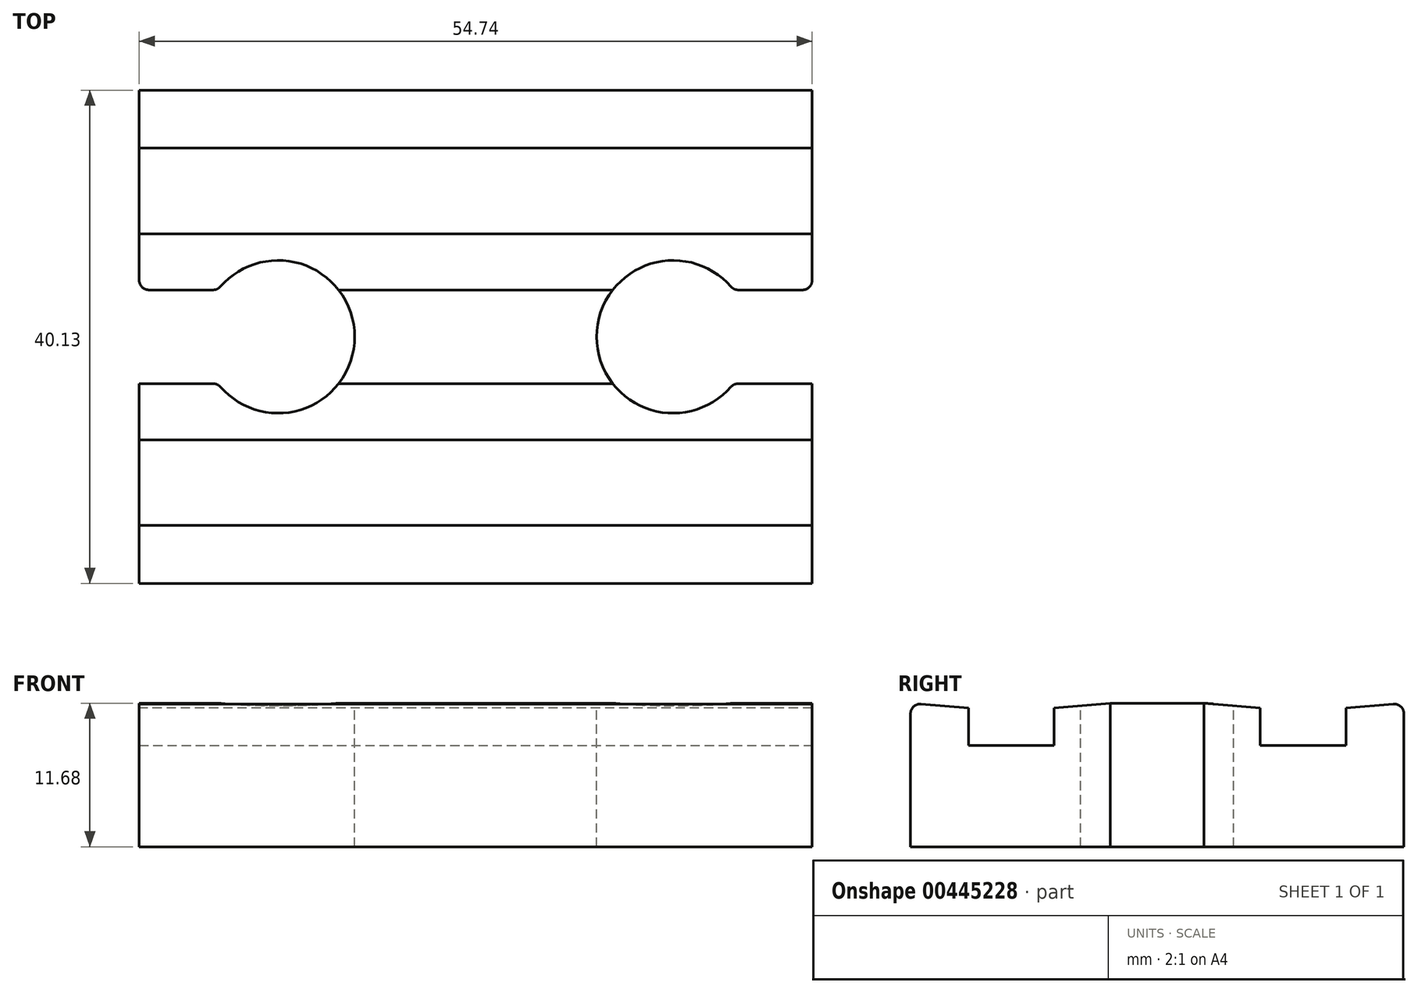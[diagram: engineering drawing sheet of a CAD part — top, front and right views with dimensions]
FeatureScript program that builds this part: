
annotation { "Feature Type Name" : "Feature", "Feature Type Description" : "" }
export const myFeature = defineFeature(function(context is Context, id is Id, definition is map)
    precondition{}
    {
        {
            var Q0;
            Q0=qCreatedBy(makeId("Top.planeOp"),FACE);
            var sketch = newSketch(context, id + "F0", { "sketchPlane" : qUnion([Q0])});
            skLineSegment(sketch, "E0.bottom", {"start": v(0, 0) * mm, "end": v(54.74, 0) * mm});
            skLineSegment(sketch, "E0.top", {"start": v(0, 40.13) * mm, "end": v(54.74, 40.13) * mm});
            skLineSegment(sketch, "E0.left", {"start": v(0, 0) * mm, "end": v(0, 40.13) * mm});
            skLineSegment(sketch, "E0.right", {"start": v(54.74, 0) * mm, "end": v(54.74, 40.13) * mm});
            skSolve(sketch);
        }
        {
            var Q0;
            Q0 = qSketchRegion(id + "F0", true);
            extrude(context, id + "F1", {"entities" : qUnion([Q0]), "depth" : 11.68 * mm});
        }
        {
            var Q0;
            Q0=makeQuery(id+"F1.opExtrude","SWEPT_FACE",FACE,{"disambiguationData":[OSD([sQuery(id+"F0.wireOp",EDGE,"E0.right")])]});
            var sketch = newSketch(context, id + "F2", { "sketchPlane" : qUnion([Q0])});
            skLineSegment(sketch, "E1.bottom", {"start": v(35.4, 11.68) * mm, "end": v(28.45, 11.68) * mm});
            skLineSegment(sketch, "E1.top", {"start": v(35.4, 8.26) * mm, "end": v(28.45, 8.26) * mm});
            skLineSegment(sketch, "E1.left", {"start": v(35.4, 11.68) * mm, "end": v(35.4, 8.26) * mm});
            skLineSegment(sketch, "E1.right", {"start": v(28.45, 11.68) * mm, "end": v(28.45, 8.26) * mm});
            skLineSegment(sketch, "E2", {"start": v(20.07, 11.68) * mm, "end": v(20.07, 0) * mm, "construction": true});
            skLineSegment(sketch, "E3.MirrorCS", {"start": v(11.68, 11.68) * mm, "end": v(11.68, 8.26) * mm});
            skLineSegment(sketch, "E4.MirrorCS", {"start": v(4.72, 11.68) * mm, "end": v(11.68, 11.68) * mm});
            skLineSegment(sketch, "E5.MirrorCS", {"start": v(4.72, 8.26) * mm, "end": v(11.68, 8.26) * mm});
            skLineSegment(sketch, "E6.MirrorCS", {"start": v(4.72, 11.68) * mm, "end": v(4.72, 8.26) * mm});
            skSolve(sketch);
        }
        {
            var Q0;
            Q0 = qSketchRegion(id + "F2", true);
            extrude(context, id + "F3", {"entities" : qUnion([Q0]), "operationType" : NewBodyOperationType.REMOVE, "endBound" : BoundingType.THROUGH_ALL, "oppositeDirection" : true, "depth" : 25.4 * mm});
        }
        {
            var Q0;
            Q0=makeQuery(id+"F1.opExtrude","SWEPT_FACE",FACE,{"disambiguationData":[OSD([sQuery(id+"F0.wireOp",EDGE,"E0.right")])]});
            var sketch = newSketch(context, id + "F4", { "sketchPlane" : qUnion([Q0])});
            skLineSegment(sketch, "E7", {"start": v(0, 11.68) * mm, "end": v(4.72, 11.29) * mm});
            skLineSegment(sketch, "E8", {"start": v(40.13, 11.68) * mm, "end": v(35.4, 11.29) * mm});
            skLineSegment(sketch, "E9", {"start": v(0, 11.68) * mm, "end": v(4.72, 11.68) * mm});
            skLineSegment(sketch, "E10", {"start": v(4.72, 11.68) * mm, "end": v(4.72, 11.29) * mm});
            skLineSegment(sketch, "E11", {"start": v(35.4, 11.29) * mm, "end": v(35.4, 11.68) * mm});
            skLineSegment(sketch, "E12", {"start": v(35.4, 11.68) * mm, "end": v(40.13, 11.68) * mm});
            skSolve(sketch);
        }
        {
            var Q0;
            Q0 = qSketchRegion(id + "F4", true);
            extrude(context, id + "F5", {"entities" : qUnion([Q0]), "operationType" : NewBodyOperationType.REMOVE, "endBound" : BoundingType.THROUGH_ALL, "oppositeDirection" : true, "depth" : 25.4 * mm});
        }
        {
            var Q0;
            {var subQ0=sQuery(id+"F0.wireOp",EDGE,"E0.left");var subQ1=sQuery(id+"F0.wireOp",EDGE,"E0.right");Q0=makeQuery(id+"F3.boolean.opBoolean","SPLIT",FACE,{"disambiguationData":[TD([makeQuery(id+"F3.opExtrude","SWEPT_FACE",FACE,{"disambiguationData":[OSD([sQuery(id+"F2.wireOp",EDGE,"E1.right")])]})])],"derivedFrom":makeQuery(id+"F1.opExtrude","CAP_FACE",FACE,{"disambiguationData":[OSD([sQuery(id+"F0.wireOp",EDGE,"E0.bottom"),sQuery(id+"F0.wireOp",EDGE,"E0.top"),subQ0,subQ1])],"isStart":false})});}
            var sketch = newSketch(context, id + "F6", { "sketchPlane" : qUnion([Q0])});
            skLineSegment(sketch, "E13", {"start": v(0, 20.07) * mm, "end": v(54.74, 20.07) * mm, "construction": true});
            skArc(sketch, "E14", {"start": v(6.38, 16.26) * mm, "mid": v(17.53, 20.07) * mm, "end": v(6.38, 23.88) * mm});
            skArc(sketch, "E15", {"start": v(48.35, 23.88) * mm, "mid": v(37.21, 20.07) * mm, "end": v(48.35, 16.26) * mm});
            skLineSegment(sketch, "E16.bottom", {"start": v(0, 23.88) * mm, "end": v(6.38, 23.88) * mm});
            skLineSegment(sketch, "E16.top", {"start": v(0, 16.26) * mm, "end": v(6.38, 16.26) * mm});
            skLineSegment(sketch, "E16.left", {"start": v(0, 23.88) * mm, "end": v(0, 16.26) * mm});
            skLineSegment(sketch, "E17.bottom", {"start": v(48.35, 23.88) * mm, "end": v(54.74, 23.88) * mm});
            skLineSegment(sketch, "E17.top", {"start": v(48.35, 16.26) * mm, "end": v(54.74, 16.26) * mm});
            skLineSegment(sketch, "E17.right", {"start": v(54.74, 23.88) * mm, "end": v(54.74, 16.26) * mm});
            skLineSegment(sketch, "E18", {"start": v(6.38, 23.88) * mm, "end": v(6.38, 20.07) * mm, "construction": true});
            skLineSegment(sketch, "E19", {"start": v(6.38, 16.26) * mm, "end": v(6.38, 20.07) * mm, "construction": true});
            skLineSegment(sketch, "E20", {"start": v(17.53, 28.45) * mm, "end": v(17.53, 11.68) * mm, "construction": true});
            skSolve(sketch);
        }
        {
            var Q0;
            Q0 = qSketchRegion(id + "F6", true);
            extrude(context, id + "F7", {"entities" : qUnion([Q0]), "operationType" : NewBodyOperationType.REMOVE, "endBound" : BoundingType.THROUGH_ALL, "oppositeDirection" : true, "depth" : 25.4 * mm});
        }
        {
            var Q0;
            {var subQ1=sQuery(id+"F0.wireOp",EDGE,"E0.left");var subQ3=sQuery(id+"F0.wireOp",EDGE,"E0.bottom");Q0=makeQuery(id+"F7.boolean.opBoolean","SPLIT",FACE,{"disambiguationData":[TD([makeQuery(id+"F1.opExtrude","SWEPT_FACE",FACE,{"disambiguationData":[OSD([subQ3])]})])],"derivedFrom":makeQuery(id+"F1.opExtrude","SWEPT_FACE",FACE,{"disambiguationData":[OSD([subQ1])]})});}
            var sketch = newSketch(context, id + "F8", { "sketchPlane" : qUnion([Q0])});
            skLineSegment(sketch, "E21", {"start": v(-23.88, 11.68) * mm, "end": v(-28.45, 11.29) * mm});
            skLineSegment(sketch, "E22", {"start": v(-11.68, 11.29) * mm, "end": v(-16.26, 11.68) * mm});
            skLineSegment(sketch, "E23", {"start": v(-28.45, 11.29) * mm, "end": v(-28.45, 11.68) * mm});
            skLineSegment(sketch, "E24", {"start": v(-28.45, 11.68) * mm, "end": v(-23.88, 11.68) * mm});
            skLineSegment(sketch, "E25", {"start": v(-11.68, 11.29) * mm, "end": v(-11.68, 11.68) * mm});
            skLineSegment(sketch, "E26", {"start": v(-11.68, 11.68) * mm, "end": v(-16.26, 11.68) * mm});
            skSolve(sketch);
        }
        {
            var Q0;
            Q0 = qSketchRegion(id + "F8", true);
            extrude(context, id + "F9", {"entities" : qUnion([Q0]), "operationType" : NewBodyOperationType.REMOVE, "endBound" : BoundingType.THROUGH_ALL, "oppositeDirection" : true, "depth" : 25.4 * mm});
        }
        {
            var Q0;
            {var subQ0=sQuery(id+"F0.wireOp",EDGE,"E0.top");Q0=makeQuery(id+"F5.boolean.opBoolean","MERGE",EDGE,{"derivedFrom":[makeQuery(id+"F1.opExtrude","CAP_EDGE",EDGE,{"disambiguationData":[OSD([subQ0])],"isStart":false}),makeQuery(id+"F5.opExtrude","SWEPT_EDGE",EDGE,{"disambiguationData":[OSD([subQ0,sQuery(id+"F0.wireOp",EDGE,"E0.right"),sQuery(id+"F4.wireOp",EDGE,"E8"),sQuery(id+"F4.wireOp",EDGE,"E12")])]})]});}
            var Q1;
            Q1=makeQuery(id+"F5.boolean.opBoolean","COPY",EDGE,{"derivedFrom":makeQuery(id+"F5.opExtrude","SWEPT_EDGE",EDGE,{"disambiguationData":[OSD([sQuery(id+"F2.wireOp",EDGE,"E1.left"),sQuery(id+"F4.wireOp",EDGE,"E8"),sQuery(id+"F4.wireOp",EDGE,"E11")])]})});
            var Q2;
            Q2=makeQuery(id+"F9.boolean.opBoolean","COPY",EDGE,{"derivedFrom":makeQuery(id+"F9.opExtrude","SWEPT_EDGE",EDGE,{"disambiguationData":[OSD([sQuery(id+"F8.wireOp",EDGE,"E21"),sQuery(id+"F8.wireOp",EDGE,"E23")])]})});
            var Q3;
            Q3=makeQuery(id+"F9.boolean.opBoolean","COPY",EDGE,{"derivedFrom":makeQuery(id+"F9.opExtrude","SWEPT_EDGE",EDGE,{"disambiguationData":[OSD([sQuery(id+"F0.wireOp",EDGE,"E0.left"),sQuery(id+"F2.wireOp",EDGE,"E3.MirrorCS"),sQuery(id+"F8.wireOp",EDGE,"E22"),sQuery(id+"F8.wireOp",EDGE,"E25")])]})});
            var Q4;
            Q4=makeQuery(id+"F5.boolean.opBoolean","COPY",EDGE,{"derivedFrom":makeQuery(id+"F5.opExtrude","SWEPT_EDGE",EDGE,{"disambiguationData":[OSD([sQuery(id+"F2.wireOp",EDGE,"E6.MirrorCS"),sQuery(id+"F4.wireOp",EDGE,"E7"),sQuery(id+"F4.wireOp",EDGE,"E10")])]})});
            var Q5;
            {var subQ0=sQuery(id+"F0.wireOp",EDGE,"E0.bottom");Q5=makeQuery(id+"F5.boolean.opBoolean","MERGE",EDGE,{"derivedFrom":[makeQuery(id+"F1.opExtrude","CAP_EDGE",EDGE,{"disambiguationData":[OSD([subQ0])],"isStart":false}),makeQuery(id+"F5.opExtrude","SWEPT_EDGE",EDGE,{"disambiguationData":[OSD([subQ0,sQuery(id+"F0.wireOp",EDGE,"E0.right"),sQuery(id+"F4.wireOp",EDGE,"E7"),sQuery(id+"F4.wireOp",EDGE,"E9")])]})]});}
            var Q6;
            Q6=makeQuery(id+"F7.boolean.opBoolean","COPY",EDGE,{"derivedFrom":makeQuery(id+"F7.opExtrude","SWEPT_EDGE",EDGE,{"disambiguationData":[OSD([sQuery(id+"F0.wireOp",EDGE,"E0.right"),sQuery(id+"F6.wireOp",EDGE,"E17.top"),sQuery(id+"F6.wireOp",EDGE,"E17.right")])]})});
            var Q7;
            Q7=makeQuery(id+"F7.boolean.opBoolean","COPY",EDGE,{"derivedFrom":makeQuery(id+"F7.opExtrude","SWEPT_EDGE",EDGE,{"disambiguationData":[OSD([sQuery(id+"F0.wireOp",EDGE,"E0.right"),sQuery(id+"F6.wireOp",EDGE,"E17.bottom"),sQuery(id+"F6.wireOp",EDGE,"E17.right")])]})});
            var Q8;
            Q8=makeQuery(id+"F7.boolean.opBoolean","COPY",EDGE,{"derivedFrom":makeQuery(id+"F7.opExtrude","SWEPT_EDGE",EDGE,{"disambiguationData":[OSD([sQuery(id+"F0.wireOp",EDGE,"E0.left"),sQuery(id+"F6.wireOp",EDGE,"E16.bottom"),sQuery(id+"F6.wireOp",EDGE,"E16.left")])]})});
            var Q9;
            Q9=makeQuery(id+"F7.boolean.opBoolean","COPY",EDGE,{"derivedFrom":makeQuery(id+"F7.opExtrude","SWEPT_EDGE",EDGE,{"disambiguationData":[OSD([sQuery(id+"F0.wireOp",EDGE,"E0.left"),sQuery(id+"F6.wireOp",EDGE,"E16.top"),sQuery(id+"F6.wireOp",EDGE,"E16.left")])]})});
            var Q10;
            Q10=makeQuery(id+"F7.boolean.opBoolean","COPY",EDGE,{"derivedFrom":makeQuery(id+"F7.opExtrude","SWEPT_EDGE",EDGE,{"disambiguationData":[OSD([sQuery(id+"F6.wireOp",EDGE,"E14"),sQuery(id+"F6.wireOp",EDGE,"E16.bottom")])]})});
            var Q11;
            Q11=makeQuery(id+"F7.boolean.opBoolean","COPY",EDGE,{"derivedFrom":makeQuery(id+"F7.opExtrude","SWEPT_EDGE",EDGE,{"disambiguationData":[OSD([sQuery(id+"F6.wireOp",EDGE,"E14"),sQuery(id+"F6.wireOp",EDGE,"E16.top")])]})});
            var Q12;
            Q12=makeQuery(id+"F7.boolean.opBoolean","COPY",EDGE,{"derivedFrom":makeQuery(id+"F7.opExtrude","SWEPT_EDGE",EDGE,{"disambiguationData":[OSD([sQuery(id+"F6.wireOp",EDGE,"E15"),sQuery(id+"F6.wireOp",EDGE,"E17.top")])]})});
            var Q13;
            Q13=makeQuery(id+"F7.boolean.opBoolean","COPY",EDGE,{"derivedFrom":makeQuery(id+"F7.opExtrude","SWEPT_EDGE",EDGE,{"disambiguationData":[OSD([sQuery(id+"F6.wireOp",EDGE,"E15"),sQuery(id+"F6.wireOp",EDGE,"E17.bottom")])]})});
            fillet(context, id + "F10", {"entities" : qUnion([Q0, Q1, Q2, Q3, Q4, Q5, Q6, Q7, Q8, Q9, Q10, Q11, Q12, Q13]), "radius" : 0.8 * mm, "tangentPropagation" : true, "allowEdgeOverflow" : false});
        }
    });
